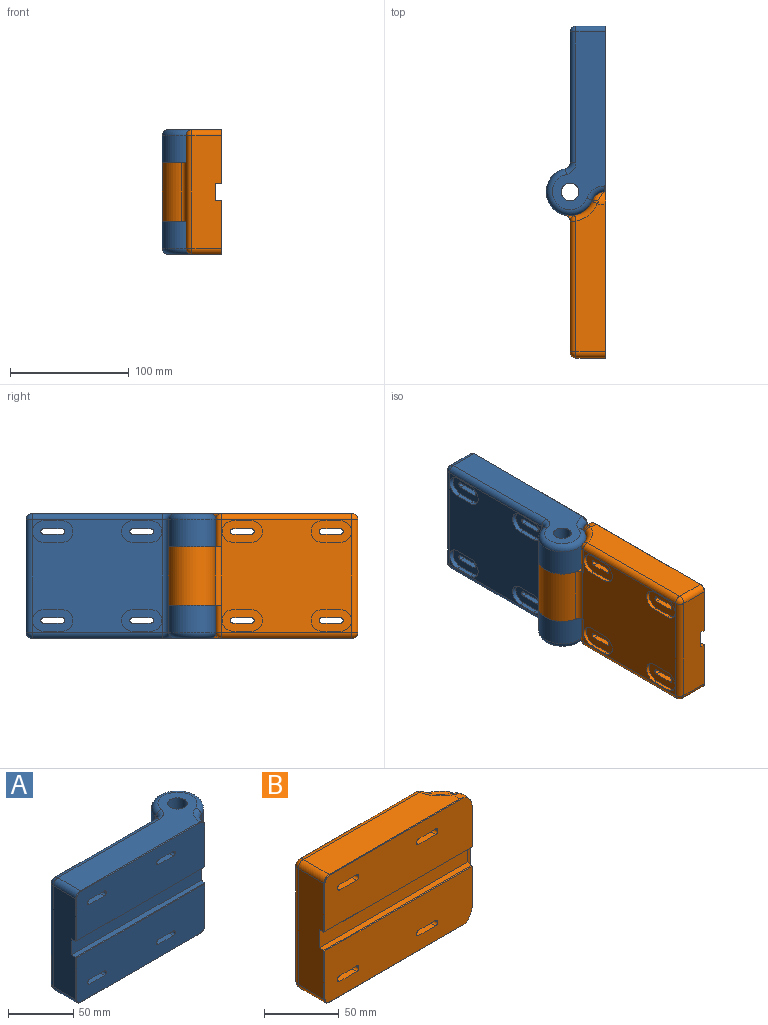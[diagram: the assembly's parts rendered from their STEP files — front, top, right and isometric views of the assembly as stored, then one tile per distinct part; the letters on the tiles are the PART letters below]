
ASSEMBLY  parts=2 mates=1
PART A: 99 faces, bbox 161.6x51.6x105 mm
  f0: plane 26x0.5mm, normal (-1,0,0), area 13mm2, adj f1,f7,f45,f98
  f1: cylinder r=2mm len=26mm, axis (0,1,0), area 81.7mm2, adj f0,f2,f45,f98
  f2: plane 26x16mm, normal (0,0,1), area 416mm2, adj f1,f3,f45,f98
  f3: cylinder r=2mm len=26mm, axis (0,1,0), area 81.7mm2, adj f2,f4,f45,f98
  f4: plane 26x0.5mm, normal (1,0,0), area 13mm2, adj f3,f5,f45,f98
  f5: cylinder r=2mm len=26mm, axis (0,1,0), area 81.7mm2, adj f4,f6,f45,f98
  f6: plane 26x16mm, normal (0,0,-1), area 416mm2, adj f5,f7,f45,f98
  f7: cylinder r=2mm len=26mm, axis (0,1,0), area 81.7mm2, adj f0,f6,f45,f98
  f8: plane 26x0.5mm, normal (-1,0,0), area 13mm2, adj f9,f15,f45,f93
  f9: cylinder r=2mm len=26mm, axis (0,1,0), area 81.7mm2, adj f8,f10,f45,f93
  f10: plane 26x16mm, normal (0,0,1), area 416mm2, adj f9,f11,f45,f93
  f11: cylinder r=2mm len=26mm, axis (0,1,0), area 81.7mm2, adj f10,f12,f45,f93
  f12: plane 26x0.5mm, normal (1,0,0), area 13mm2, adj f11,f13,f45,f93
  f13: cylinder r=2mm len=26mm, axis (0,1,0), area 81.7mm2, adj f12,f14,f45,f93
  f14: plane 26x16mm, normal (0,0,-1), area 416mm2, adj f13,f15,f45,f93
  f15: cylinder r=2mm len=26mm, axis (0,1,0), area 81.7mm2, adj f8,f14,f45,f93
  f16: plane 26x16mm, normal (0,0,1), area 416mm2, adj f17,f23,f37,f88
  f17: cylinder r=2mm len=26mm, axis (0,1,0), area 81.7mm2, adj f16,f18,f37,f88
  f18: plane 26x0.5mm, normal (1,0,0), area 13mm2, adj f17,f19,f37,f88
  f19: cylinder r=2mm len=26mm, axis (0,1,0), area 81.7mm2, adj f18,f20,f37,f88
  f20: plane 26x16mm, normal (0,0,-1), area 416mm2, adj f19,f21,f37,f88
  f21: cylinder r=2mm len=26mm, axis (0,1,0), area 81.7mm2, adj f20,f22,f37,f88
  f22: plane 26x0.5mm, normal (-1,0,0), area 13mm2, adj f21,f23,f37,f88
  f23: cylinder r=2mm len=26mm, axis (0,1,0), area 81.7mm2, adj f16,f22,f37,f88
  f24: plane 26x0.5mm, normal (-1,0,0), area 13mm2, adj f25,f31,f37,f83
  f25: cylinder r=2mm len=26mm, axis (0,1,0), area 81.7mm2, adj f24,f26,f37,f83
  f26: plane 26x16mm, normal (0,0,1), area 416mm2, adj f25,f27,f37,f83
  f27: cylinder r=2mm len=26mm, axis (0,1,0), area 81.7mm2, adj f26,f28,f37,f83
  f28: plane 26x0.5mm, normal (1,0,0), area 13mm2, adj f27,f29,f37,f83
  f29: cylinder r=2mm len=26mm, axis (0,1,0), area 81.7mm2, adj f28,f30,f37,f83
  f30: plane 26x16mm, normal (0,0,-1), area 416mm2, adj f29,f31,f37,f83
  f31: cylinder r=2mm len=26mm, axis (0,1,0), area 81.7mm2, adj f24,f30,f37,f83
  f32: cylinder r=20mm len=39.6mm, axis (0,0,-1), area 1908.2mm2, adj f34,f35,f50,f59
  f33: cylinder r=7.5mm len=28mm, axis (0,0,-1), area 1319.5mm2, adj f42,f50
  f34: cylinder r=11mm len=95mm, axis (0,0,-1), area 1108.6mm2, adj f32,f36,f40,f44,f46,f47,f48,f49
  f35: cylinder r=5mm len=95mm, axis (0,0,-1), area 580.7mm2, adj f32,f38,f40,f49,f50,f51,f53,f58
  f36: plane 40x0.52mm, normal (1,0,0), area 20.7mm2, adj f34,f48,f56,f67
  f37: plane 139x44mm, normal (0,-1,0), area 5934.2mm2, adj f16,f17,f18,f19,f20,f21,f22,f23
  f38: plane 110.51x95mm, normal (0,1,0), area 8328.1mm2, adj f35,f52,f57,f64,f79,f80,f81,f82
  f39: plane 95x24.5mm, normal (-1,0,0), area 2260mm2, adj f46,f47,f48,f62,f64,f66,f71,f76
  f40: cylinder r=20mm len=39.6mm, axis (0,0,-1), area 1908.2mm2, adj f34,f35,f51,f54
  f41: cylinder r=7.5mm len=28mm, axis (0,0,-1), area 1319.5mm2, adj f43,f51
  f42: plane 150x44.5mm, normal (0,0,1), area 3714.9mm2, adj f33,f57,f58,f59,f60,f61,f66,f74
  f43: plane 150x44.5mm, normal (0,0,-1), area 3714.9mm2, adj f41,f52,f53,f54,f55,f56,f62,f69
  f44: plane 40x0.52mm, normal (1,0,0), area 20.7mm2, adj f34,f46,f61,f72
  f45: plane 139x44mm, normal (0,-1,0), area 5934.2mm2, adj f0,f1,f2,f3,f4,f5,f6,f7
  f46: plane 140.75x4.5mm, normal (0,0,-1), area 631mm2, adj f34,f39,f44,f47,f77
  f47: plane 140.75x15mm, normal (0,-1,0), area 2111.2mm2, adj f34,f39,f46,f48
  f48: plane 140.75x4.5mm, normal (0,0,1), area 631mm2, adj f34,f36,f39,f47,f78
  f49: cylinder r=20.25mm len=49mm, axis (0,0,-1), area 1957.1mm2, adj f34,f35,f50,f51
  f50: plane 40.25x40.25mm, normal (0,0,-1), area 1090.1mm2, adj f32,f33,f34,f35,f49
  f51: plane 40.25x40.25mm, normal (0,0,1), area 1090.1mm2, adj f34,f35,f40,f41,f49
  f52: cylinder r=5mm len=110.51mm, axis (-1,0,0), area 867.9mm2, adj f38,f43,f53,f63
  f53: torus R=10mm, axis (0,0,1), area 73.3mm2, adj f35,f43,f52,f54
  f54: torus R=15mm, axis (0,0,1), area 592.4mm2, adj f40,f43,f53,f55
  f55: torus R=16mm, axis (0,0,1), area 121.6mm2, adj f34,f43,f54,f56
  f56: cylinder r=5mm len=5mm, axis (0,-1,0), area 4.1mm2, adj f36,f43,f55,f68
  f57: cylinder r=5mm len=110.51mm, axis (1,0,0), area 867.9mm2, adj f38,f42,f58,f65
  f58: torus R=10mm, axis (0,0,1), area 73.3mm2, adj f35,f42,f57,f59
  f59: torus R=15mm, axis (0,0,1), area 592.4mm2, adj f32,f42,f58,f60
  f60: torus R=16mm, axis (0,0,1), area 121.6mm2, adj f34,f42,f59,f61
  f61: cylinder r=5mm len=5mm, axis (0,1,0), area 4.1mm2, adj f42,f44,f60,f73
  f62: cylinder r=5mm len=24.5mm, axis (0,-1,0), area 192.4mm2, adj f39,f43,f63,f70
  f63: sphere r=5mm, area 39.3mm2, adj f52,f62,f64
  f64: cylinder r=5mm len=95mm, axis (0,0,-1), area 746.1mm2, adj f38,f39,f63,f65
  f65: sphere r=5mm, area 39.3mm2, adj f57,f64,f66
  f66: cylinder r=5mm len=24.5mm, axis (0,1,0), area 192.4mm2, adj f39,f42,f65,f75
  f67: plane 40x0.5mm, normal (0.71,-0.71,0), area 28.1mm2, adj f36,f37,f68,f78
  f68: cone r=4.5mm half-angle=45deg, axis (0,1,0), area 5.3mm2, adj f37,f56,f67,f69
  f69: plane 130x0.5mm, normal (0,-0.71,-0.71), area 91.9mm2, adj f37,f43,f68,f70
  f70: cone r=4.5mm half-angle=45deg, axis (0,1,0), area 5.3mm2, adj f37,f62,f69,f71
  f71: plane 40x0.5mm, normal (-0.71,-0.71,0), area 28.1mm2, adj f37,f39,f70,f78
  f72: plane 40x0.5mm, normal (0.71,-0.71,0), area 28.1mm2, adj f44,f45,f73,f77
  f73: cone r=4.5mm half-angle=45deg, axis (0,1,0), area 5.3mm2, adj f45,f61,f72,f74
  f74: plane 130x0.5mm, normal (0,-0.71,0.71), area 91.9mm2, adj f42,f45,f73,f75
  f75: cone r=4.5mm half-angle=45deg, axis (0,1,0), area 5.3mm2, adj f45,f66,f74,f76
  f76: plane 40x0.5mm, normal (-0.71,-0.71,0), area 28.1mm2, adj f39,f45,f75,f77
  f77: plane 140x0.5mm, normal (0,-0.71,-0.71), area 98.6mm2, adj f45,f46,f72,f76
  f78: plane 140x0.5mm, normal (0,-0.71,0.71), area 98.6mm2, adj f37,f48,f67,f71
  f79: plane 16x4mm, normal (0,0,-1), area 64mm2, adj f38,f80,f82,f83
  f80: cylinder r=9mm len=18mm, axis (0,1,0), area 113.1mm2, adj f38,f79,f81,f83
  f81: plane 16x4mm, normal (0,0,1), area 64mm2, adj f38,f80,f82,f83
  f82: cylinder r=9mm len=18mm, axis (0,1,0), area 113.1mm2, adj f38,f79,f81,f83
  f83: plane 34x18mm, normal (0,1,0), area 455.9mm2, adj f24,f25,f26,f27,f28,f29,f30,f31
  f84: plane 16x4mm, normal (0,0,-1), area 64mm2, adj f38,f85,f87,f88
  f85: cylinder r=9mm len=18mm, axis (0,1,0), area 113.1mm2, adj f38,f84,f86,f88
  f86: plane 16x4mm, normal (0,0,1), area 64mm2, adj f38,f85,f87,f88
  f87: cylinder r=9mm len=18mm, axis (0,1,0), area 113.1mm2, adj f38,f84,f86,f88
  f88: plane 34x18mm, normal (0,1,0), area 455.9mm2, adj f16,f17,f18,f19,f20,f21,f22,f23
  f89: plane 16x4mm, normal (0,0,-1), area 64mm2, adj f38,f90,f92,f93
  f90: cylinder r=9mm len=18mm, axis (0,1,0), area 113.1mm2, adj f38,f89,f91,f93
  f91: plane 16x4mm, normal (0,0,1), area 64mm2, adj f38,f90,f92,f93
  f92: cylinder r=9mm len=18mm, axis (0,1,0), area 113.1mm2, adj f38,f89,f91,f93
  f93: plane 34x18mm, normal (0,1,0), area 455.9mm2, adj f8,f9,f10,f11,f12,f13,f14,f15
  f94: plane 16x4mm, normal (0,0,-1), area 64mm2, adj f38,f95,f97,f98
  f95: cylinder r=9mm len=18mm, axis (0,1,0), area 113.1mm2, adj f38,f94,f96,f98
  f96: plane 16x4mm, normal (0,0,1), area 64mm2, adj f38,f95,f97,f98
  f97: cylinder r=9mm len=18mm, axis (0,1,0), area 113.1mm2, adj f38,f94,f96,f98
  f98: plane 34x18mm, normal (0,1,0), area 455.9mm2, adj f0,f1,f2,f3,f4,f5,f6,f7
PART B: 100 faces, bbox 160x50.6x105.1 mm
  f0: plane 27x0.5mm, normal (-1,0,0), area 13.5mm2, adj f1,f7,f41,f99
  f1: cylinder r=2mm len=27mm, axis (0,1,0), area 84.8mm2, adj f0,f2,f41,f99
  f2: plane 27x16mm, normal (0,0,1), area 432mm2, adj f1,f3,f41,f99
  f3: cylinder r=2mm len=27mm, axis (0,1,0), area 84.8mm2, adj f2,f4,f41,f99
  f4: plane 27x0.5mm, normal (1,0,0), area 13.5mm2, adj f3,f5,f41,f99
  f5: cylinder r=2mm len=27mm, axis (0,1,0), area 84.8mm2, adj f4,f6,f41,f99
  f6: plane 27x16mm, normal (0,0,-1), area 432mm2, adj f5,f7,f41,f99
  f7: cylinder r=2mm len=27mm, axis (0,1,0), area 84.8mm2, adj f0,f6,f41,f99
  f8: plane 27x0.5mm, normal (-1,0,0), area 13.5mm2, adj f9,f15,f41,f94
  f9: cylinder r=2mm len=27mm, axis (0,1,0), area 84.8mm2, adj f8,f10,f41,f94
  f10: plane 27x16mm, normal (0,0,1), area 432mm2, adj f9,f11,f41,f94
  f11: cylinder r=2mm len=27mm, axis (0,1,0), area 84.8mm2, adj f10,f12,f41,f94
  f12: plane 27x0.5mm, normal (1,0,0), area 13.5mm2, adj f11,f13,f41,f94
  f13: cylinder r=2mm len=27mm, axis (0,1,0), area 84.8mm2, adj f12,f14,f41,f94
  f14: plane 27x16mm, normal (0,0,-1), area 432mm2, adj f13,f15,f41,f94
  f15: cylinder r=2mm len=27mm, axis (0,1,0), area 84.8mm2, adj f8,f14,f41,f94
  f16: plane 27x16mm, normal (0,0,1), area 432mm2, adj f17,f23,f37,f89
  f17: cylinder r=2mm len=27mm, axis (0,1,0), area 84.8mm2, adj f16,f18,f37,f89
  f18: plane 27x0.5mm, normal (1,0,0), area 13.5mm2, adj f17,f19,f37,f89
  f19: cylinder r=2mm len=27mm, axis (0,1,0), area 84.8mm2, adj f18,f20,f37,f89
  f20: plane 27x16mm, normal (0,0,-1), area 432mm2, adj f19,f21,f37,f89
  f21: cylinder r=2mm len=27mm, axis (0,1,0), area 84.8mm2, adj f20,f22,f37,f89
  f22: plane 27x0.5mm, normal (-1,0,0), area 13.5mm2, adj f21,f23,f37,f89
  f23: cylinder r=2mm len=27mm, axis (0,1,0), area 84.8mm2, adj f16,f22,f37,f89
  f24: plane 27x0.5mm, normal (-1,0,0), area 13.5mm2, adj f25,f31,f37,f84
  f25: cylinder r=2mm len=27mm, axis (0,1,0), area 84.8mm2, adj f24,f26,f37,f84
  f26: plane 27x16mm, normal (0,0,1), area 432mm2, adj f25,f27,f37,f84
  f27: cylinder r=2mm len=27mm, axis (0,1,0), area 84.8mm2, adj f26,f28,f37,f84
  f28: plane 27x0.5mm, normal (1,0,0), area 13.5mm2, adj f27,f29,f37,f84
  f29: cylinder r=2mm len=27mm, axis (0,1,0), area 84.8mm2, adj f28,f30,f37,f84
  f30: plane 27x16mm, normal (0,0,-1), area 432mm2, adj f29,f31,f37,f84
  f31: cylinder r=2mm len=27mm, axis (0,1,0), area 84.8mm2, adj f24,f30,f37,f84
  f32: plane 124.94x24.5mm, normal (0,0,1), area 2878.6mm2, adj f52,f57,f61,f66,f79
  f33: cylinder r=20mm len=49mm, axis (0,0,-1), area 4044.1mm2, adj f45,f46,f48,f50
  f34: cylinder r=7.5mm len=49mm, axis (0,0,-1), area 2309.1mm2, adj f48,f50
  f35: plane 124.94x24.5mm, normal (0,0,-1), area 2878.6mm2, adj f51,f53,f58,f69,f75
  f36: plane 34.16x0.34mm, normal (1,0,0), area 11.3mm2, adj f37,f45,f65,f75
  f37: plane 139.54x44.04mm, normal (0,-1,0), area 5939mm2, adj f16,f17,f18,f19,f20,f21,f22,f23
  f38: plane 110.51x95mm, normal (0,1,0), area 8316.4mm2, adj f46,f48,f50,f51,f52,f55,f68,f71
  f39: plane 95x24.5mm, normal (-1,0,0), area 2260mm2, adj f42,f43,f44,f53,f55,f57,f60,f63
  f40: plane 34.16x0.34mm, normal (1,0,0), area 11.3mm2, adj f41,f45,f64,f79
  f41: plane 139.54x44.04mm, normal (0,-1,0), area 5939mm2, adj f0,f1,f2,f3,f4,f5,f6,f7
  f42: plane 140.94x4.5mm, normal (0,0,-1), area 631.4mm2, adj f39,f43,f45,f64
  f43: plane 140.94x15mm, normal (0,-1,0), area 2114.2mm2, adj f39,f42,f44,f45
  f44: plane 140.94x4.5mm, normal (0,0,1), area 631.4mm2, adj f39,f43,f45,f65
  f45: cylinder r=12mm len=83mm, axis (0,0,-1), area 633mm2, adj f33,f36,f40,f42,f43,f44,f48,f50
  f46: cylinder r=5mm len=49mm, axis (0,0,-1), area 335.5mm2, adj f33,f38,f48,f50
  f47: cylinder r=20.25mm len=23mm, axis (0,0,-1), area 471.2mm2, adj f48,f69,f71,f72,f74
  f48: plane 49.45x44.75mm, normal (0,0,-1), area 1125mm2, adj f33,f34,f38,f45,f46,f47,f71,f72
  f49: cylinder r=20.25mm len=23mm, axis (0,0,-1), area 471.2mm2, adj f50,f66,f68,f76,f77
  f50: plane 49.45x44.75mm, normal (0,0,1), area 1125mm2, adj f33,f34,f38,f45,f46,f49,f68,f76
  f51: cylinder r=5mm len=110.25mm, axis (-1,0,0), area 865.9mm2, adj f35,f38,f54,f70
  f52: cylinder r=5mm len=110.25mm, axis (1,0,0), area 865.9mm2, adj f32,f38,f56,f67
  f53: cylinder r=5mm len=24.5mm, axis (0,-1,0), area 192.4mm2, adj f35,f39,f54,f59
  f54: sphere r=5mm, area 39.3mm2, adj f51,f53,f55
  f55: cylinder r=5mm len=95mm, axis (0,0,-1), area 746.1mm2, adj f38,f39,f54,f56
  f56: sphere r=5mm, area 39.3mm2, adj f52,f55,f57
  f57: cylinder r=5mm len=24.5mm, axis (0,1,0), area 192.4mm2, adj f32,f39,f56,f62
  f58: plane 127.28x0.5mm, normal (0,-0.71,-0.71), area 89.2mm2, adj f35,f37,f59,f75
  f59: cone r=4.5mm half-angle=45deg, axis (0,1,0), area 5.3mm2, adj f37,f53,f58,f60
  f60: plane 40x0.5mm, normal (-0.71,-0.71,0), area 28.1mm2, adj f37,f39,f59,f65
  f61: plane 127.28x0.5mm, normal (0,-0.71,0.71), area 89.2mm2, adj f32,f41,f62,f79
  f62: cone r=4.5mm half-angle=45deg, axis (0,1,0), area 5.3mm2, adj f41,f57,f61,f63
  f63: plane 40x0.5mm, normal (-0.71,-0.71,0), area 28.1mm2, adj f39,f41,f62,f64
  f64: plane 140x0.5mm, normal (0,-0.71,-0.71), area 98.8mm2, adj f40,f41,f42,f45,f63
  f65: plane 140x0.5mm, normal (0,-0.71,0.71), area 98.8mm2, adj f36,f37,f44,f45,f60
  f66: torus R=25.25mm, axis (0,0,1), area 166.7mm2, adj f32,f49,f67,f77
  f67: sphere r=5mm, area 34.3mm2, adj f52,f66,f68
  f68: cylinder r=5mm len=23mm, axis (0,0,-1), area 157.7mm2, adj f38,f49,f50,f67
  f69: torus R=25.25mm, axis (0,0,1), area 166.7mm2, adj f35,f47,f70,f74
  f70: sphere r=5mm, area 34.3mm2, adj f51,f69,f71
  f71: cylinder r=5mm len=23mm, axis (0,0,-1), area 157.7mm2, adj f38,f47,f48,f70
  f72: cylinder r=11mm len=22.87mm, axis (0,0,1), area 277.9mm2, adj f45,f47,f48,f73
  f73: bspline ~10.75x10.49mm, area 71mm2, adj f72,f74,f75
  f74: bspline ~6.02x5.62mm, area 14mm2, adj f47,f69,f73,f75
  f75: torus R=23mm, axis (0,0,1), area 63.3mm2, adj f35,f36,f37,f45,f58,f73,f74
  f76: cylinder r=11mm len=22.87mm, axis (0,0,1), area 277.9mm2, adj f45,f49,f50,f78
  f77: bspline ~6.02x5.62mm, area 14mm2, adj f49,f66,f78,f79
  f78: bspline ~10.75x10.49mm, area 71mm2, adj f76,f77,f79
  f79: torus R=23mm, axis (0,0,1), area 63.3mm2, adj f32,f40,f41,f45,f61,f77,f78
  f80: cylinder r=9mm len=18mm, axis (0,1,0), area 84.8mm2, adj f38,f81,f83,f84
  f81: plane 16x3mm, normal (0,0,-1), area 48mm2, adj f38,f80,f82,f84
  f82: cylinder r=9mm len=18mm, axis (0,1,0), area 84.8mm2, adj f38,f81,f83,f84
  f83: plane 16x3mm, normal (0,0,1), area 48mm2, adj f38,f80,f82,f84
  f84: plane 34x18mm, normal (0,1,0), area 455.9mm2, adj f24,f25,f26,f27,f28,f29,f30,f31
  f85: cylinder r=9mm len=18mm, axis (0,1,0), area 84.8mm2, adj f38,f86,f88,f89
  f86: plane 16x3mm, normal (0,0,-1), area 48mm2, adj f38,f85,f87,f89
  f87: cylinder r=9mm len=18mm, axis (0,1,0), area 84.8mm2, adj f38,f86,f88,f89
  f88: plane 16x3mm, normal (0,0,1), area 48mm2, adj f38,f85,f87,f89
  f89: plane 34x18mm, normal (0,1,0), area 455.9mm2, adj f16,f17,f18,f19,f20,f21,f22,f23
  f90: cylinder r=9mm len=18mm, axis (0,1,0), area 84.8mm2, adj f38,f91,f93,f94
  f91: plane 16x3mm, normal (0,0,-1), area 48mm2, adj f38,f90,f92,f94
  f92: cylinder r=9mm len=18mm, axis (0,1,0), area 84.8mm2, adj f38,f91,f93,f94
  f93: plane 16x3mm, normal (0,0,1), area 48mm2, adj f38,f90,f92,f94
  f94: plane 34x18mm, normal (0,1,0), area 455.9mm2, adj f8,f9,f10,f11,f12,f13,f14,f15
  f95: plane 16x3mm, normal (0,0,-1), area 48mm2, adj f38,f96,f98,f99
  f96: cylinder r=9mm len=18mm, axis (0,1,0), area 84.8mm2, adj f38,f95,f97,f99
  f97: plane 16x3mm, normal (0,0,1), area 48mm2, adj f38,f96,f98,f99
  f98: cylinder r=9mm len=18mm, axis (0,1,0), area 84.8mm2, adj f38,f95,f97,f99
  f99: plane 34x18mm, normal (0,1,0), area 455.9mm2, adj f0,f1,f2,f3,f4,f5,f6,f7
PLACE A rot(axis=(-0.71,0.71,0),180deg) t=(-23.04,125.13,74.79)mm
PLACE B rot(axis=(0,0,1),90deg) t=(-23.04,125.13,-30.21)mm
MATE cylindrical A.f49 <-> B.f33  axis (0,0,1) through (-23.04,125.13,-2.21)mm
